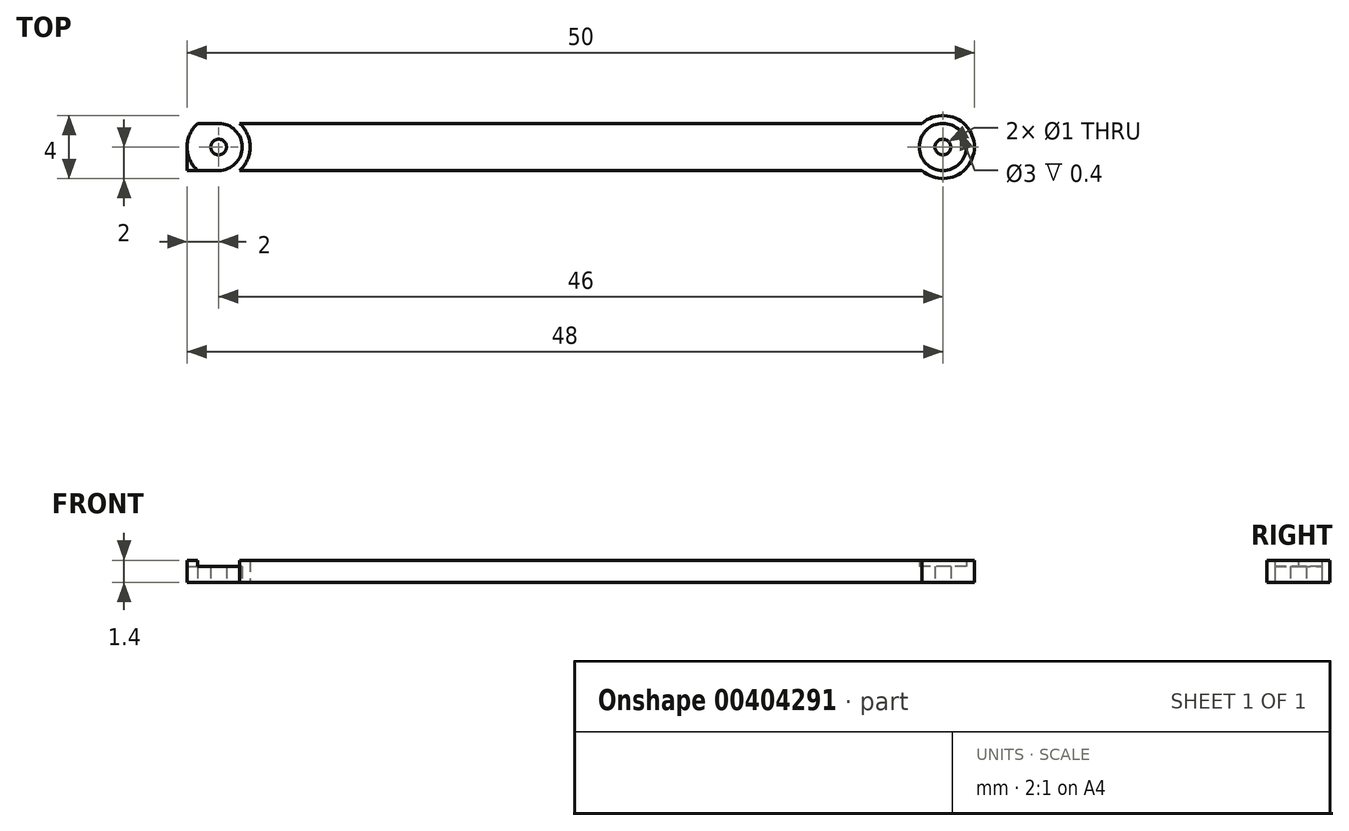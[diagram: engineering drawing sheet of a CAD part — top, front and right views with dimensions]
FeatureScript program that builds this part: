
annotation { "Feature Type Name" : "Feature", "Feature Type Description" : "" }
export const myFeature = defineFeature(function(context is Context, id is Id, definition is map)
    precondition{}
    {
        {
            var Q0;
            Q0=qCreatedBy(makeId("Top.planeOp"),FACE);
            var sketch = newSketch(context, id + "F0", { "sketchPlane" : qUnion([Q0])});
            skLineSegment(sketch, "E0.bottom", {"start": v(-25, -1.5) * mm, "end": v(25, -1.5) * mm});
            skLineSegment(sketch, "E0.top", {"start": v(-25, 1.5) * mm, "end": v(25, 1.5) * mm});
            skLineSegment(sketch, "E0.left", {"start": v(-25, -1.5) * mm, "end": v(-25, 1.5) * mm});
            skLineSegment(sketch, "E0.right", {"start": v(25, -1.5) * mm, "end": v(25, 1.5) * mm});
            skPoint(sketch, "E0.middle", {"position": v(0, 0) * mm});
            skCircle(sketch, "E1", {"center": v(-23, 0) * mm, "radius": 2 * mm});
            skCircle(sketch, "E2", {"center": v(-23, 0) * mm, "radius": 0.5 * mm});
            skCircle(sketch, "E3", {"center": v(23, 0) * mm, "radius": 2 * mm});
            skCircle(sketch, "E4", {"center": v(23, 0) * mm, "radius": 0.5 * mm});
            skCircle(sketch, "E5", {"center": v(23, 0) * mm, "radius": 1.5 * mm});
            skCircle(sketch, "E6", {"center": v(-23, 0) * mm, "radius": 1.5 * mm});
            skSolve(sketch);
        }
        {
            var Q0;
            Q0=makeQuery(id+"F0.imprint","IMPRINT",FACE,{"disambiguationData":[TD([[makeQuery(id+"F0.imprint","IMPRINT",EDGE,{"derivedFrom":sQuery(id+"F0.wireOp",EDGE,"E2")}),-1.0]])]});
            var Q1;
            {var subQ0=sQuery(id+"F0.wireOp",EDGE,"E1");var subQ1=sQuery(id+"F0.wireOp",EDGE,"E0.bottom");var subQ2=makeQuery(id+"F0.imprint","INTERSECT",VERTEX,{"disambiguationData":[OD(0.0)],"derivedFrom":[subQ1,subQ0]});Q1=makeQuery(id+"F0.imprint","IMPRINT",FACE,{"disambiguationData":[TD([[makeQuery(id+"F0.imprint","IMPRINT",EDGE,{"disambiguationData":[TD([[subQ2,-1.0]])],"derivedFrom":subQ1}),-1.0]])]});}
            var Q2;
            {var subQ0=sQuery(id+"F0.wireOp",EDGE,"E1");var subQ1=sQuery(id+"F0.wireOp",EDGE,"E0.top");var subQ2=makeQuery(id+"F0.imprint","INTERSECT",VERTEX,{"disambiguationData":[OD(0.0)],"derivedFrom":[subQ1,subQ0]});Q2=makeQuery(id+"F0.imprint","IMPRINT",FACE,{"disambiguationData":[TD([[makeQuery(id+"F0.imprint","IMPRINT",EDGE,{"disambiguationData":[TD([[subQ2,-1.0]])],"derivedFrom":subQ1}),1.0]])]});}
            var Q3;
            {var subQ0=sQuery(id+"F0.wireOp",EDGE,"E1");var subQ1=sQuery(id+"F0.wireOp",EDGE,"E0.bottom");var subQ2=makeQuery(id+"F0.imprint","INTERSECT",VERTEX,{"disambiguationData":[OD(1.0)],"derivedFrom":[subQ1,subQ0]});Q3=makeQuery(id+"F0.imprint","IMPRINT",FACE,{"disambiguationData":[TD([[makeQuery(id+"F0.imprint","IMPRINT",EDGE,{"disambiguationData":[TD([[subQ2,-1.0]])],"derivedFrom":subQ1}),1.0]])]});}
            var Q4;
            Q4=makeQuery(id+"F0.imprint","IMPRINT",FACE,{"disambiguationData":[TD([[makeQuery(id+"F0.imprint","IMPRINT",EDGE,{"derivedFrom":sQuery(id+"F0.wireOp",EDGE,"E4")}),-1.0]])]});
            var Q5;
            {var subQ0=sQuery(id+"F0.wireOp",EDGE,"E3");var subQ1=sQuery(id+"F0.wireOp",EDGE,"E0.bottom");var subQ2=makeQuery(id+"F0.imprint","INTERSECT",VERTEX,{"disambiguationData":[OD(0.0)],"derivedFrom":[subQ1,subQ0]});Q5=makeQuery(id+"F0.imprint","IMPRINT",FACE,{"disambiguationData":[TD([[makeQuery(id+"F0.imprint","IMPRINT",EDGE,{"disambiguationData":[TD([[subQ2,-1.0]])],"derivedFrom":subQ1}),-1.0]])]});}
            var Q6;
            {var subQ0=sQuery(id+"F0.wireOp",EDGE,"E3");var subQ1=sQuery(id+"F0.wireOp",EDGE,"E0.top");var subQ2=makeQuery(id+"F0.imprint","INTERSECT",VERTEX,{"disambiguationData":[OD(0.0)],"derivedFrom":[subQ1,subQ0]});Q6=makeQuery(id+"F0.imprint","IMPRINT",FACE,{"disambiguationData":[TD([[makeQuery(id+"F0.imprint","IMPRINT",EDGE,{"disambiguationData":[TD([[subQ2,-1.0]])],"derivedFrom":subQ1}),1.0]])]});}
            var Q7;
            {var subQ0=sQuery(id+"F0.wireOp",EDGE,"E3");var subQ1=sQuery(id+"F0.wireOp",EDGE,"E0.bottom");var subQ2=makeQuery(id+"F0.imprint","INTERSECT",VERTEX,{"disambiguationData":[OD(0.0)],"derivedFrom":[subQ1,subQ0]});Q7=makeQuery(id+"F0.imprint","IMPRINT",FACE,{"disambiguationData":[TD([[makeQuery(id+"F0.imprint","IMPRINT",EDGE,{"disambiguationData":[TD([[subQ2,-1.0]])],"derivedFrom":subQ1}),1.0]])]});}
            var Q8;
            {var subQ0=sQuery(id+"F0.wireOp",EDGE,"E3");var subQ1=sQuery(id+"F0.wireOp",EDGE,"E0.bottom");var subQ2=makeQuery(id+"F0.imprint","INTERSECT",VERTEX,{"disambiguationData":[OD(1.0)],"derivedFrom":[subQ1,subQ0]});Q8=makeQuery(id+"F0.imprint","IMPRINT",FACE,{"disambiguationData":[TD([[makeQuery(id+"F0.imprint","IMPRINT",EDGE,{"disambiguationData":[TD([[subQ2,1.0]])],"derivedFrom":subQ1}),1.0]])]});}
            var Q9;
            {var subQ0=sQuery(id+"F0.wireOp",EDGE,"E1");var subQ1=sQuery(id+"F0.wireOp",EDGE,"E0.bottom");var subQ2=makeQuery(id+"F0.imprint","INTERSECT",VERTEX,{"disambiguationData":[OD(0.0)],"derivedFrom":[subQ1,subQ0]});Q9=makeQuery(id+"F0.imprint","IMPRINT",FACE,{"disambiguationData":[TD([[makeQuery(id+"F0.imprint","IMPRINT",EDGE,{"disambiguationData":[TD([[subQ2,-1.0]])],"derivedFrom":subQ1}),1.0]])]});}
            var Q10;
            {var subQ0=sQuery(id+"F0.wireOp",EDGE,"E1");var subQ1=sQuery(id+"F0.wireOp",EDGE,"E0.bottom");var subQ2=makeQuery(id+"F0.imprint","INTERSECT",VERTEX,{"disambiguationData":[OD(1.0)],"derivedFrom":[subQ1,subQ0]});Q10=makeQuery(id+"F0.imprint","IMPRINT",FACE,{"disambiguationData":[TD([[makeQuery(id+"F0.imprint","IMPRINT",EDGE,{"disambiguationData":[TD([[subQ2,1.0]])],"derivedFrom":subQ1}),1.0]])]});}
            extrude(context, id + "F1", {"entities" : qUnion([Q0, Q1, Q2, Q3, Q4, Q5, Q6, Q7, Q8, Q9, Q10]), "depth" : 1 * mm});
        }
        {
            var Q0;
            {var subQ0=sQuery(id+"F0.wireOp",EDGE,"E1");var subQ1=sQuery(id+"F0.wireOp",EDGE,"E0.bottom");var subQ2=makeQuery(id+"F0.imprint","INTERSECT",VERTEX,{"disambiguationData":[OD(0.0)],"derivedFrom":[subQ1,subQ0]});Q0=makeQuery(id+"F0.imprint","IMPRINT",FACE,{"disambiguationData":[TD([[makeQuery(id+"F0.imprint","IMPRINT",EDGE,{"disambiguationData":[TD([[subQ2,-1.0]])],"derivedFrom":subQ1}),-1.0]])]});}
            var Q1;
            {var subQ0=sQuery(id+"F0.wireOp",EDGE,"E1");var subQ1=sQuery(id+"F0.wireOp",EDGE,"E0.bottom");var subQ2=makeQuery(id+"F0.imprint","INTERSECT",VERTEX,{"disambiguationData":[OD(0.0)],"derivedFrom":[subQ1,subQ0]});Q1=makeQuery(id+"F0.imprint","IMPRINT",FACE,{"disambiguationData":[TD([[makeQuery(id+"F0.imprint","IMPRINT",EDGE,{"disambiguationData":[TD([[subQ2,-1.0]])],"derivedFrom":subQ1}),1.0]])]});}
            var Q2;
            {var subQ0=sQuery(id+"F0.wireOp",EDGE,"E1");var subQ1=sQuery(id+"F0.wireOp",EDGE,"E0.bottom");var subQ2=makeQuery(id+"F0.imprint","INTERSECT",VERTEX,{"disambiguationData":[OD(1.0)],"derivedFrom":[subQ1,subQ0]});Q2=makeQuery(id+"F0.imprint","IMPRINT",FACE,{"disambiguationData":[TD([[makeQuery(id+"F0.imprint","IMPRINT",EDGE,{"disambiguationData":[TD([[subQ2,1.0]])],"derivedFrom":subQ1}),1.0]])]});}
            var Q3;
            {var subQ0=sQuery(id+"F0.wireOp",EDGE,"E1");var subQ1=sQuery(id+"F0.wireOp",EDGE,"E0.top");var subQ2=makeQuery(id+"F0.imprint","INTERSECT",VERTEX,{"disambiguationData":[OD(0.0)],"derivedFrom":[subQ1,subQ0]});Q3=makeQuery(id+"F0.imprint","IMPRINT",FACE,{"disambiguationData":[TD([[makeQuery(id+"F0.imprint","IMPRINT",EDGE,{"disambiguationData":[TD([[subQ2,-1.0]])],"derivedFrom":subQ1}),1.0]])]});}
            var Q4;
            {var subQ0=sQuery(id+"F0.wireOp",EDGE,"E3");var subQ1=sQuery(id+"F0.wireOp",EDGE,"E0.bottom");var subQ2=makeQuery(id+"F0.imprint","INTERSECT",VERTEX,{"disambiguationData":[OD(0.0)],"derivedFrom":[subQ1,subQ0]});Q4=makeQuery(id+"F0.imprint","IMPRINT",FACE,{"disambiguationData":[TD([[makeQuery(id+"F0.imprint","IMPRINT",EDGE,{"disambiguationData":[TD([[subQ2,-1.0]])],"derivedFrom":subQ1}),-1.0]])]});}
            var Q5;
            {var subQ0=sQuery(id+"F0.wireOp",EDGE,"E3");var subQ1=sQuery(id+"F0.wireOp",EDGE,"E0.bottom");var subQ2=makeQuery(id+"F0.imprint","INTERSECT",VERTEX,{"disambiguationData":[OD(1.0)],"derivedFrom":[subQ1,subQ0]});Q5=makeQuery(id+"F0.imprint","IMPRINT",FACE,{"disambiguationData":[TD([[makeQuery(id+"F0.imprint","IMPRINT",EDGE,{"disambiguationData":[TD([[subQ2,1.0]])],"derivedFrom":subQ1}),1.0]])]});}
            var Q6;
            {var subQ0=sQuery(id+"F0.wireOp",EDGE,"E3");var subQ1=sQuery(id+"F0.wireOp",EDGE,"E0.top");var subQ2=makeQuery(id+"F0.imprint","INTERSECT",VERTEX,{"disambiguationData":[OD(0.0)],"derivedFrom":[subQ1,subQ0]});Q6=makeQuery(id+"F0.imprint","IMPRINT",FACE,{"disambiguationData":[TD([[makeQuery(id+"F0.imprint","IMPRINT",EDGE,{"disambiguationData":[TD([[subQ2,-1.0]])],"derivedFrom":subQ1}),1.0]])]});}
            var Q7;
            {var subQ0=sQuery(id+"F0.wireOp",EDGE,"E3");var subQ1=sQuery(id+"F0.wireOp",EDGE,"E0.bottom");var subQ2=makeQuery(id+"F0.imprint","INTERSECT",VERTEX,{"disambiguationData":[OD(0.0)],"derivedFrom":[subQ1,subQ0]});Q7=makeQuery(id+"F0.imprint","IMPRINT",FACE,{"disambiguationData":[TD([[makeQuery(id+"F0.imprint","IMPRINT",EDGE,{"disambiguationData":[TD([[subQ2,-1.0]])],"derivedFrom":subQ1}),1.0]])]});}
            extrude(context, id + "F2", {"entities" : qUnion([Q0, Q1, Q2, Q3, Q4, Q5, Q6, Q7]), "operationType" : NewBodyOperationType.ADD, "depth" : 1.4 * mm});
        }
    });
